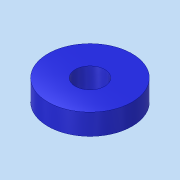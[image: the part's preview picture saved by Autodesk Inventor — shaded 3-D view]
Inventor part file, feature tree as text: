
AUTODESK INVENTOR PART (.ipt)
format: ipt  version: 2018 (Build 220112000, 112)  size: 82,944 bytes
history: native  units: mm
features: extrude x1, sketch x1
ambient origin geometry x8: Origin, YZ Plane, XZ Plane, XY Plane, X Axis, Y Axis, Z Axis, Center Point
bodies: Volumenkörper1 (feature_tree)
feature tree (2):
  extrude  "Extrusion1"  Depth=10.0mm
  sketch  "Skizze1"  dims[d0=3.5mm d1=10.0mm d2=2.5mm d3=0.0mm]
